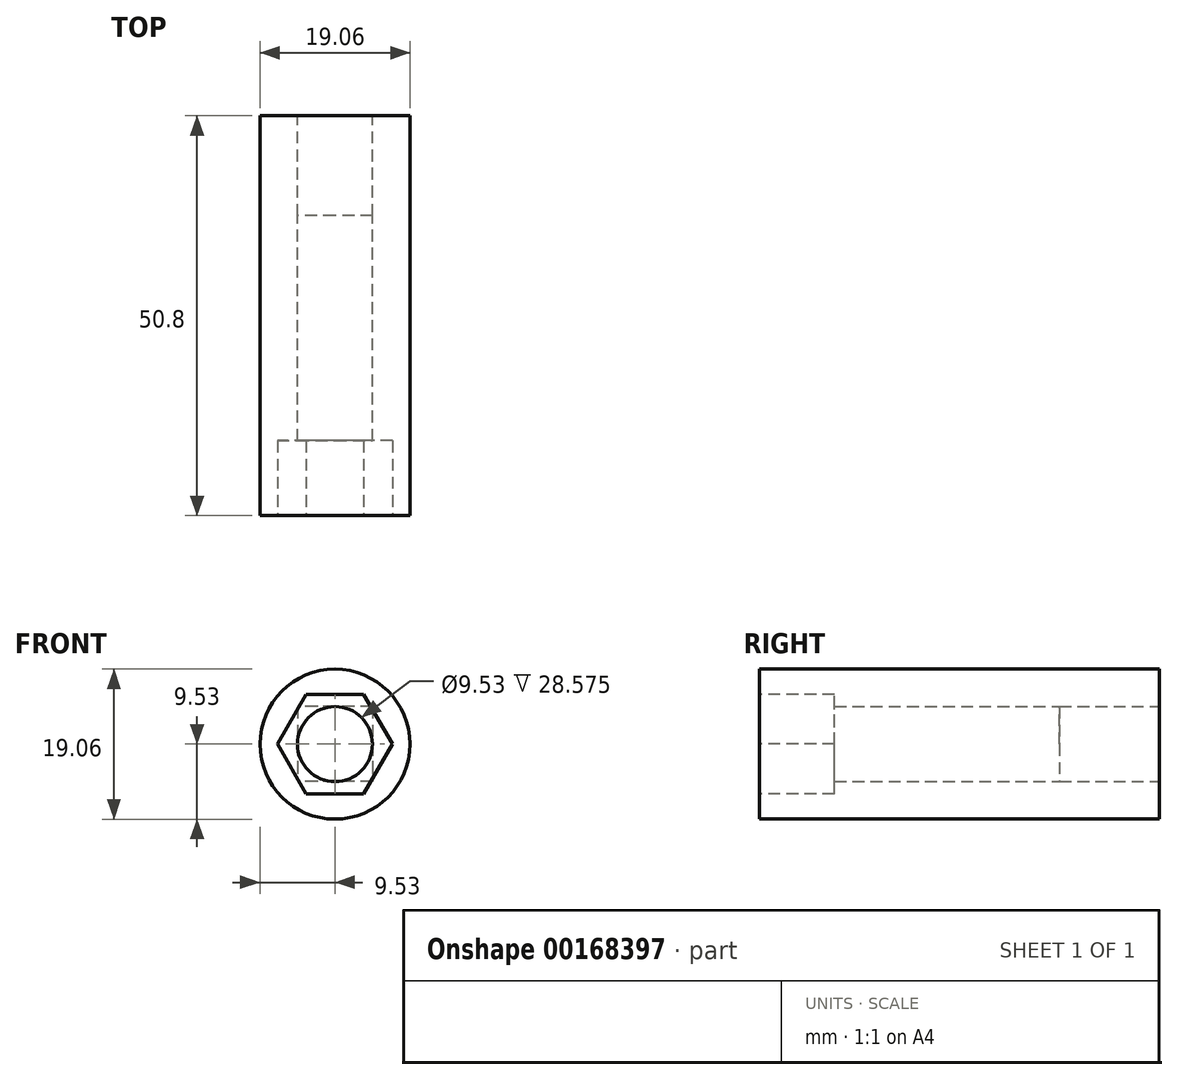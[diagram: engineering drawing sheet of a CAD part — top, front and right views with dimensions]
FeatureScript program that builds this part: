
annotation { "Feature Type Name" : "Feature", "Feature Type Description" : "" }
export const myFeature = defineFeature(function(context is Context, id is Id, definition is map)
    precondition{}
    {
        {
            var Q0;
            Q0=qCreatedBy(makeId("Front.planeOp"),FACE);
            var sketch = newSketch(context, id + "F0", { "sketchPlane" : qUnion([Q0])});
            skCircle(sketch, "E0", {"center": v(0, 0) * mm, "radius": 9.53 * mm});
            skSolve(sketch);
        }
        {
            var Q0;
            Q0 = qSketchRegion(id + "F0", true);
            extrude(context, id + "F1", {"entities" : qUnion([Q0]), "depth" : 50.8 * mm});
        }
        {
            var Q0;
            Q0=qCreatedBy(makeId("Front.planeOp"),FACE);
            var sketch = newSketch(context, id + "F2", { "sketchPlane" : qUnion([Q0])});
            skLineSegment(sketch, "E1.bottom", {"start": v(4.76, 4.76) * mm, "end": v(-4.76, 4.76) * mm});
            skLineSegment(sketch, "E1.top", {"start": v(4.76, -4.76) * mm, "end": v(-4.76, -4.76) * mm});
            skLineSegment(sketch, "E1.left", {"start": v(4.76, 4.76) * mm, "end": v(4.76, -4.76) * mm});
            skLineSegment(sketch, "E1.right", {"start": v(-4.76, 4.76) * mm, "end": v(-4.76, -4.76) * mm});
            skPoint(sketch, "E1.middle", {"position": v(0, 0) * mm});
            skCircle(sketch, "E2", {"center": v(0, 0) * mm, "radius": 4.76 * mm});
            skSolve(sketch);
        }
        {
            var Q0;
            {var subQ0=sQuery(id+"F2.wireOp",EDGE,"E2");var subQ1=makeQuery(id+"F2.imprint","INTERSECT",VERTEX,{"derivedFrom":[sQuery(id+"F2.wireOp",EDGE,"E1.bottom"),subQ0]});Q0=makeQuery(id+"F2.imprint","IMPRINT",FACE,{"disambiguationData":[TD([[makeQuery(id+"F2.imprint","IMPRINT",EDGE,{"disambiguationData":[TD([[subQ1,1.0]])],"derivedFrom":subQ0}),1.0]])]});}
            extrude(context, id + "F3", {"entities" : qUnion([Q0]), "operationType" : NewBodyOperationType.REMOVE, "endBound" : BoundingType.THROUGH_ALL, "depth" : 25.4 * mm});
        }
        {
            var Q0;
            Q0 = qSketchRegion(id + "F2", true);
            extrude(context, id + "F4", {"entities" : qUnion([Q0]), "operationType" : NewBodyOperationType.REMOVE, "depth" : 12.7 * mm});
        }
        {
            var Q0;
            Q0=makeQuery(id+"F1.opExtrude","CAP_FACE",FACE,{"disambiguationData":[OSD([sQuery(id+"F0.wireOp",EDGE,"E0")])],"isStart":false});
            var sketch = newSketch(context, id + "F5", { "sketchPlane" : qUnion([Q0])});
            skCircle(sketch, "E3.cCircle", {"center": v(0, 0) * mm, "radius": 6.32 * mm, "construction": true});
            skLineSegment(sketch, "E3.0", {"start": v(-7.3, 0) * mm, "end": v(-3.65, 6.32) * mm});
            skLineSegment(sketch, "E3.1", {"start": v(-3.65, 6.32) * mm, "end": v(3.65, 6.32) * mm});
            skLineSegment(sketch, "E3.2", {"start": v(3.65, 6.32) * mm, "end": v(7.3, 0) * mm});
            skLineSegment(sketch, "E3.3", {"start": v(7.3, 0) * mm, "end": v(3.65, -6.32) * mm});
            skLineSegment(sketch, "E3.4", {"start": v(3.65, -6.32) * mm, "end": v(-3.65, -6.32) * mm});
            skLineSegment(sketch, "E3.5", {"start": v(-3.65, -6.32) * mm, "end": v(-7.3, 0) * mm});
            skSolve(sketch);
        }
        {
            var Q0;
            Q0=makeQuery(id+"F5.imprint","IMPRINT",FACE,{"disambiguationData":[TD([[makeQuery(id+"F5.imprint","IMPRINT",EDGE,{"derivedFrom":sQuery(id+"F5.wireOp",EDGE,"E3.0")}),-1.0]])]});
            extrude(context, id + "F6", {"entities" : qUnion([Q0]), "operationType" : NewBodyOperationType.REMOVE, "oppositeDirection" : true, "depth" : 9.52 * mm});
        }
    });
